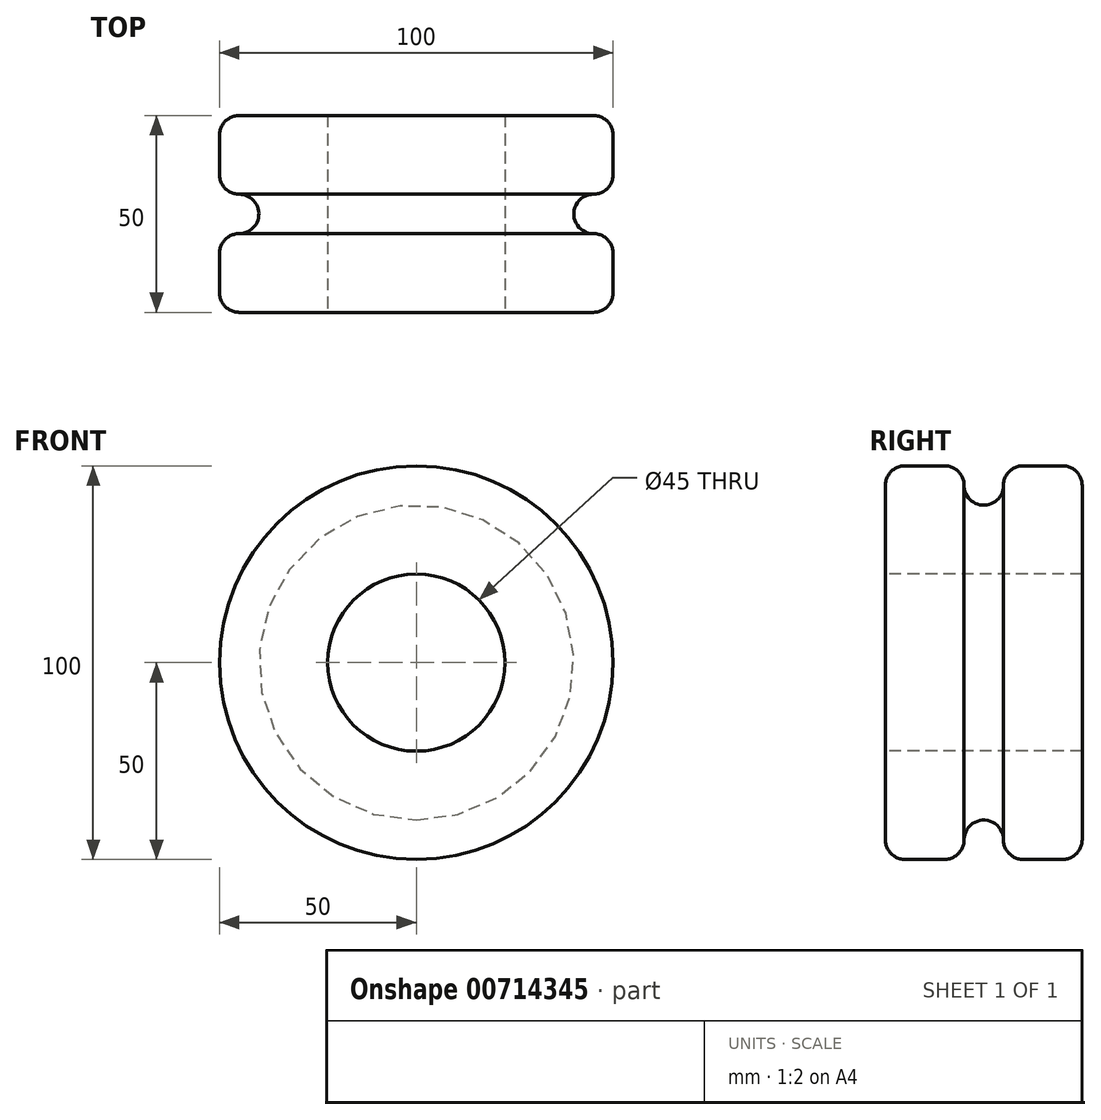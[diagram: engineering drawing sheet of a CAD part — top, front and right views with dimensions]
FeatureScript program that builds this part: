
annotation { "Feature Type Name" : "Feature", "Feature Type Description" : "" }
export const myFeature = defineFeature(function(context is Context, id is Id, definition is map)
    precondition{}
    {
        {
            var Q0;
            Q0=qCreatedBy(makeId("Top.planeOp"),FACE);
            var sketch = newSketch(context, id + "F0", { "sketchPlane" : qUnion([Q0])});
            skLineSegment(sketch, "E0", {"start": v(0, 0) * mm, "end": v(0, 50) * mm, "construction": true});
            skLineSegment(sketch, "E1", {"start": v(-22.5, 0) * mm, "end": v(-45, 0) * mm});
            skLineSegment(sketch, "E2", {"start": v(-50, 5) * mm, "end": v(-50, 15) * mm});
            skLineSegment(sketch, "E3", {"start": v(-45, 20) * mm, "end": v(-45, 20) * mm});
            skLineSegment(sketch, "E4", {"start": v(-40, 25) * mm, "end": v(-40, 25) * mm});
            skLineSegment(sketch, "E5", {"start": v(-45, 30) * mm, "end": v(-45, 30) * mm});
            skLineSegment(sketch, "E6", {"start": v(-50, 35) * mm, "end": v(-50, 45) * mm});
            skLineSegment(sketch, "E7", {"start": v(-45, 50) * mm, "end": v(-22.5, 50) * mm});
            skPoint(sketch, "E8.visualSharp", {"position": v(-50, 50) * mm});
            skArc(sketch, "E8.filletArc", {"start": v(-45, 50) * mm, "mid": v(-48.54, 48.54) * mm, "end": v(-50, 45) * mm});
            skPoint(sketch, "E9.visualSharp", {"position": v(-50, 0) * mm});
            skArc(sketch, "E9.filletArc", {"start": v(-50, 5) * mm, "mid": v(-48.54, 1.46) * mm, "end": v(-45, 0) * mm});
            skPoint(sketch, "E10.visualSharp", {"position": v(-40, 20) * mm});
            skArc(sketch, "E10.filletArc", {"start": v(-45, 20) * mm, "mid": v(-41.46, 21.46) * mm, "end": v(-40, 25) * mm});
            skPoint(sketch, "E11.visualSharp", {"position": v(-40, 30) * mm});
            skArc(sketch, "E11.filletArc", {"start": v(-40, 25) * mm, "mid": v(-41.46, 28.54) * mm, "end": v(-45, 30) * mm});
            skPoint(sketch, "E12.visualSharp", {"position": v(-50, 30) * mm});
            skArc(sketch, "E12.filletArc", {"start": v(-50, 35) * mm, "mid": v(-48.54, 31.46) * mm, "end": v(-45, 30) * mm});
            skPoint(sketch, "E13.visualSharp", {"position": v(-50, 20) * mm});
            skArc(sketch, "E13.filletArc", {"start": v(-45, 20) * mm, "mid": v(-48.54, 18.54) * mm, "end": v(-50, 15) * mm});
            skLineSegment(sketch, "E14", {"start": v(-22.5, 50) * mm, "end": v(-22.5, 0) * mm});
            skSolve(sketch);
        }
        {
            var Q0;
            Q0=makeQuery(id+"F0.imprint","IMPRINT",FACE,{"disambiguationData":[TD([[makeQuery(id+"F0.imprint","IMPRINT",EDGE,{"derivedFrom":sQuery(id+"F0.wireOp",EDGE,"E1")}),-1.0]])]});
            var Q1;
            Q1=sQuery(id+"F0.wireOp",EDGE,"E0");
            revolve(context, id + "F1", {"surfaceOperationType" : NewSurfaceOperationType.NEW, "entities" : qUnion([Q0]), "axis" : qUnion([Q1]), "revolveType" : RevolveType.FULL});
        }
    });
